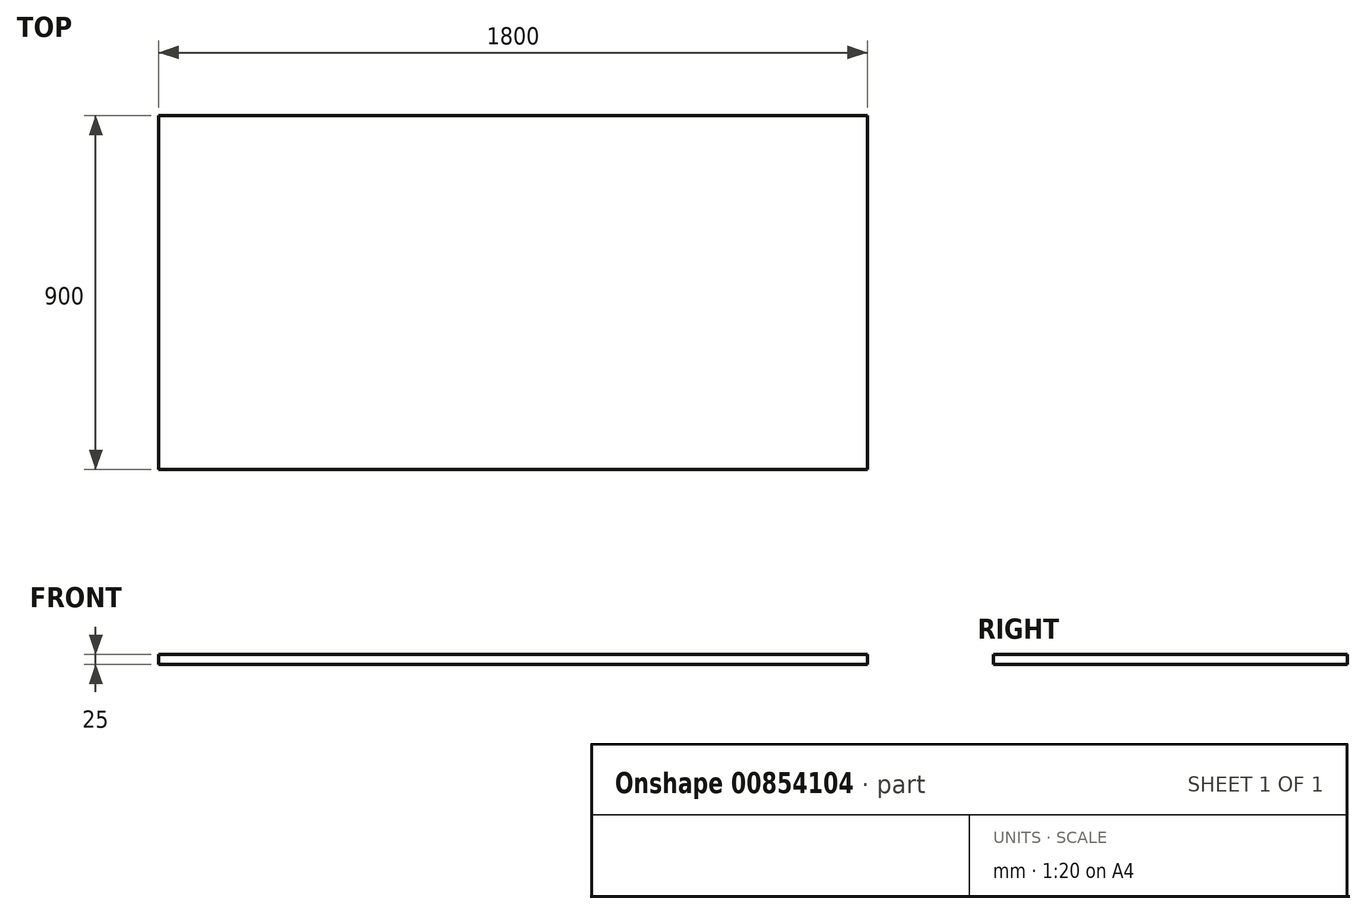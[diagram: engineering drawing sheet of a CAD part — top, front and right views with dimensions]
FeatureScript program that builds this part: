
annotation { "Feature Type Name" : "Feature", "Feature Type Description" : "" }
export const myFeature = defineFeature(function(context is Context, id is Id, definition is map)
    precondition{}
    {
        {
            var Q0;
            Q0=qCreatedBy(makeId("Top.planeOp"),FACE);
            var sketch = newSketch(context, id + "F0", { "sketchPlane" : qUnion([Q0])});
            skLineSegment(sketch, "E0.bottom", {"start": v(-1800, -450) * mm, "end": v(0, -450) * mm});
            skLineSegment(sketch, "E0.top", {"start": v(-1800, 450) * mm, "end": v(0, 450) * mm});
            skLineSegment(sketch, "E0.left", {"start": v(-1800, -450) * mm, "end": v(-1800, 450) * mm});
            skLineSegment(sketch, "E0.right", {"start": v(0, -450) * mm, "end": v(0, 450) * mm});
            skLineSegment(sketch, "E1", {"start": v(-1800, 0) * mm, "end": v(0, 0) * mm});
            skSolve(sketch);
        }
        {
            var Q0;
            Q0=makeQuery(id+"F0.imprint","IMPRINT",FACE,{"disambiguationData":[TD([[makeQuery(id+"F0.imprint","IMPRINT",EDGE,{"derivedFrom":sQuery(id+"F0.wireOp",EDGE,"E0.bottom")}),1.0]])]});
            var Q1;
            {var subQ0=sQuery(id+"F0.wireOp",EDGE,"E0.top");Q1=makeQuery(id+"F0.imprint","IMPRINT",FACE,{"disambiguationData":[TD([[makeQuery(id+"F0.imprint","IMPRINT",EDGE,{"derivedFrom":subQ0}),-1.0]])]});}
            extrude(context, id + "F1", {"entities" : qUnion([Q0, Q1]), "endBound" : BoundingType.SYMMETRIC, "depth" : 25 * mm, "offsetDistance" : 25 * mm, "hasSecondDirection" : true, "secondDirectionOppositeDirection" : true, "secondDirectionDepth" : 25 * mm});
        }
    });
